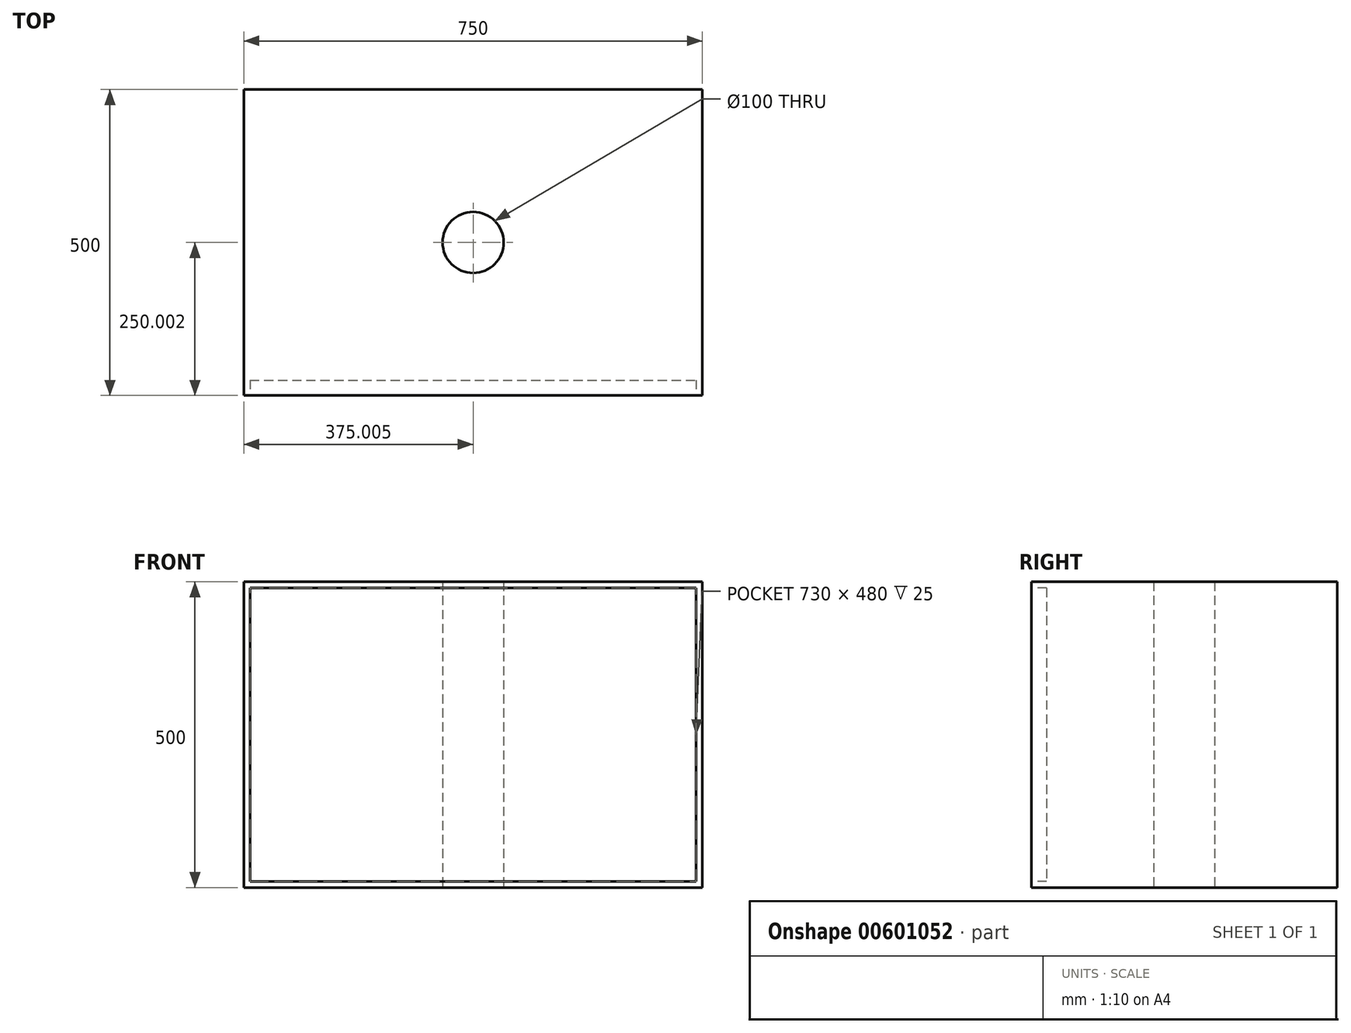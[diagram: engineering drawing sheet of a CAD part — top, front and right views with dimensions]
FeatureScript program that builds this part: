
annotation { "Feature Type Name" : "Feature", "Feature Type Description" : "" }
export const myFeature = defineFeature(function(context is Context, id is Id, definition is map)
    precondition{}
    {
        {
            var Q0;
            Q0=qCreatedBy(makeId("Top.planeOp"),FACE);
            var sketch = newSketch(context, id + "F0", { "sketchPlane" : qUnion([Q0])});
            skLineSegment(sketch, "E0.bottom", {"start": v(-66.98, 491.68) * mm, "end": v(683.02, 491.68) * mm});
            skLineSegment(sketch, "E0.top", {"start": v(-66.98, -8.32) * mm, "end": v(683.02, -8.32) * mm});
            skLineSegment(sketch, "E0.left", {"start": v(-66.98, 491.68) * mm, "end": v(-66.98, -8.32) * mm});
            skLineSegment(sketch, "E0.right", {"start": v(683.02, 491.68) * mm, "end": v(683.02, -8.32) * mm});
            skCircle(sketch, "E1", {"center": v(308.02, 241.68) * mm, "radius": 50 * mm});
            skPoint(sketch, "E1.centerSnap0", {"position": v(308.02, 491.68) * mm});
            skPoint(sketch, "E1.centerSnap1", {"position": v(-66.98, 241.68) * mm});
            skLineSegment(sketch, "E2.bottom", {"start": v(-56.98, 1.68) * mm, "end": v(673.02, 1.68) * mm});
            skLineSegment(sketch, "E2.top", {"start": v(-56.98, 481.68) * mm, "end": v(673.02, 481.68) * mm});
            skLineSegment(sketch, "E2.left", {"start": v(-56.98, 1.68) * mm, "end": v(-56.98, 481.68) * mm});
            skLineSegment(sketch, "E2.right", {"start": v(673.02, 1.68) * mm, "end": v(673.02, 481.68) * mm});
            skSolve(sketch);
        }
        {
            var Q0;
            Q0 = qSketchRegion(id + "F0", true);
            var Q1;
            Q1=makeQuery(id+"F0.imprint","IMPRINT",FACE,{"disambiguationData":[TD([[makeQuery(id+"F0.imprint","IMPRINT",EDGE,{"derivedFrom":sQuery(id+"F0.wireOp",EDGE,"E1")}),-1.0]])]});
            var Q2;
            Q2=makeQuery(id+"F0.imprint","IMPRINT",FACE,{"disambiguationData":[TD([[makeQuery(id+"F0.imprint","IMPRINT",EDGE,{"derivedFrom":sQuery(id+"F0.wireOp",EDGE,"E1")}),1.0]])]});
            extrude(context, id + "F1", {"entities" : qUnion([Q0, Q1, Q2]), "depth" : 500 * mm, "offsetDistance" : 25 * mm});
        }
        {
            var Q0;
            Q0=makeQuery(id+"F1.opExtrude","SWEPT_FACE",FACE,{"disambiguationData":[OSD([sQuery(id+"F0.wireOp",EDGE,"E0.top")])]});
            var sketch = newSketch(context, id + "F2", { "sketchPlane" : qUnion([Q0])});
            skLineSegment(sketch, "E3.bottom", {"start": v(-56.98, 490) * mm, "end": v(673.02, 490) * mm});
            skLineSegment(sketch, "E3.top", {"start": v(-56.98, 10) * mm, "end": v(673.02, 10) * mm});
            skLineSegment(sketch, "E3.left", {"start": v(-56.98, 490) * mm, "end": v(-56.98, 10) * mm});
            skLineSegment(sketch, "E3.right", {"start": v(673.02, 490) * mm, "end": v(673.02, 10) * mm});
            skSolve(sketch);
        }
        {
            var Q0;
            Q0 = qSketchRegion(id + "F2", true);
            extrude(context, id + "F3", {"entities" : qUnion([Q0]), "operationType" : NewBodyOperationType.REMOVE, "oppositeDirection" : true, "depth" : 25 * mm, "offsetDistance" : 25 * mm});
        }
        {
            var Q0;
            Q0=makeQuery(id+"F0.imprint","IMPRINT",FACE,{"disambiguationData":[TD([[makeQuery(id+"F0.imprint","IMPRINT",EDGE,{"derivedFrom":sQuery(id+"F0.wireOp",EDGE,"E1")}),1.0]])]});
            extrude(context, id + "F4", {"entities" : qUnion([Q0]), "operationType" : NewBodyOperationType.REMOVE, "depth" : 930 * mm, "offsetDistance" : 25 * mm});
        }
    });
